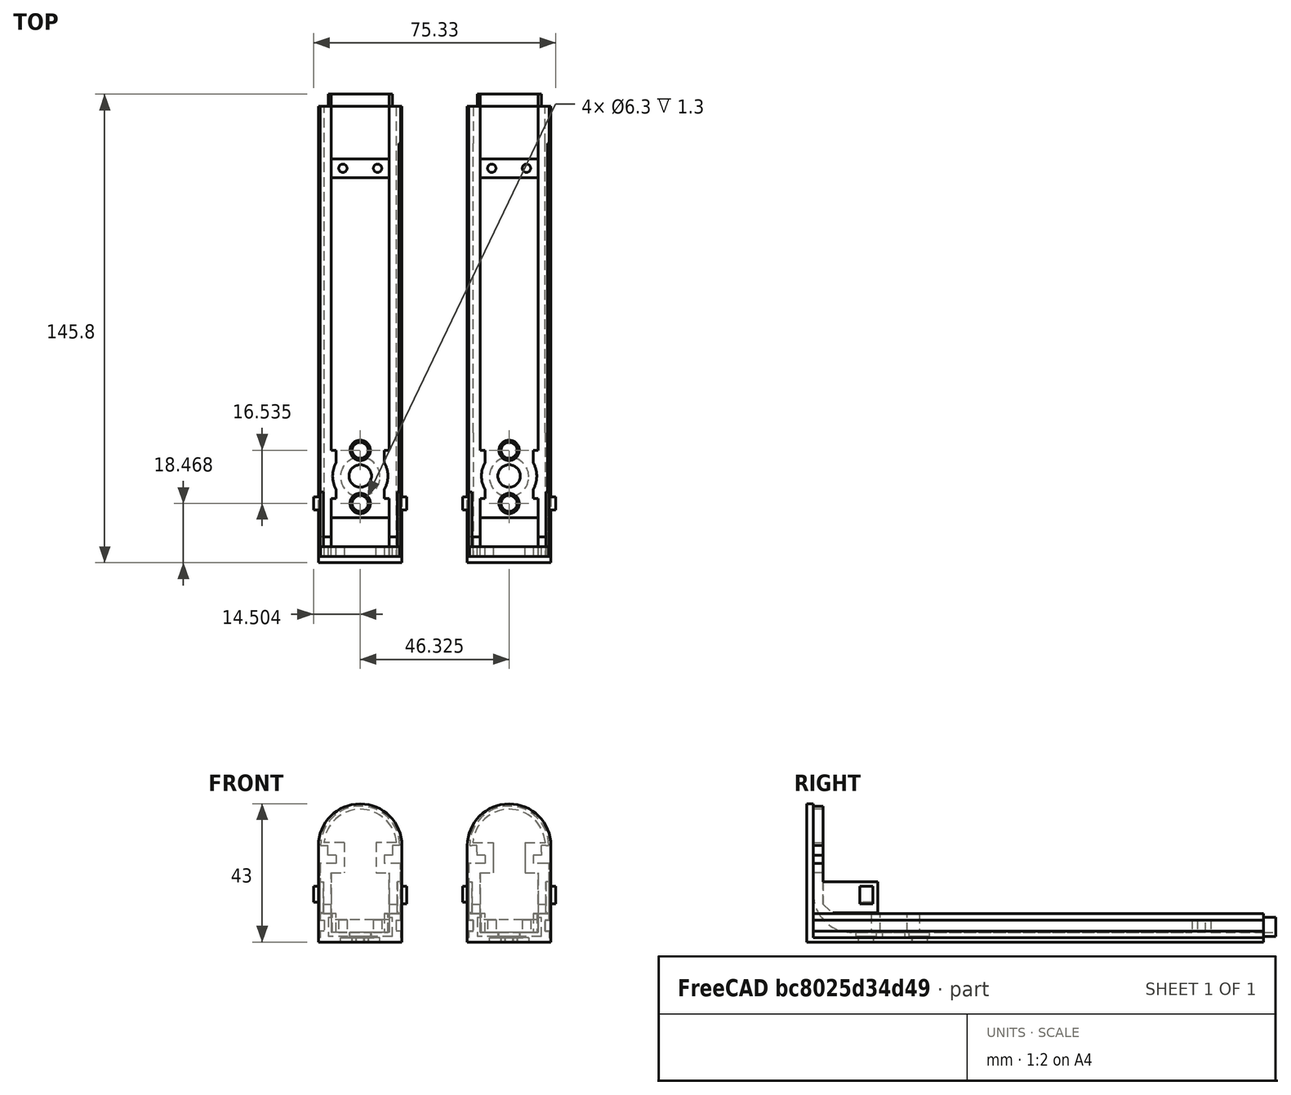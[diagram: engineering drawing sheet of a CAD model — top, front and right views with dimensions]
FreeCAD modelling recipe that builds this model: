
FCSTD DOCUMENT  (FreeCAD 0.18.3R)
Label: lamp.rail.button.section
License: All rights reserved
LicenseURL: http://en.wikipedia.org/wiki/All_rights_reserved
objects: Part::Extrusion×123, Part::Part2DObjectPython×96, Part::Cut×48, Part::Feature×34, Part::MultiFuse×28, Part::FeaturePython×8
note: 337 computed .brp shape members not serialized (recipe doc carries the construction recipe); baked Part::Feature solids carry a one-line shape summary decoded from their .brp

FEATURE [Part::Part2DObjectPython] Wire  # Draft 2D object (typed FeaturePython)
  ChamferSize = 0
  Closed = true
  End = (0.21072,-23,0.864956)
  FilletRadius = 0
  Length = 84.1989
  MakeFace = true
  Placement = pos=(0.21072,-23,6.66496) rot=(1,0,0;1.5708rad)
  Points = (20) [(0,0,0),(-4.5,0,-7.10543e-15),(-4.5,-2,-3.55271e-15),(-3.25,-2,-3.55271e-15),(-3.25,-5.4,-3.55271e-15),(-4.5,-5.4,-3.55271e-15),+14 more]
  Start = (0.21072,-23,6.66496)
  Subdivisions = 0
FEATURE [Part::Extrusion] Extrude018
  Base = -> Wire
  Dir = (-1e-16,-1,2e-16)
  DirMode = 2
  FaceMakerClass = Part::FaceMakerBullseye
  LengthFwd = 50
  LengthRev = 0
  Placement = pos=(37.158,39.9631,-2.99945) rot=(0,0,1;0rad)
  Solid = false
  Symmetric = false
FEATURE [Part::Part2DObjectPython] Circle  # Draft 2D object (typed FeaturePython)
  FirstAngle = 0
  LastAngle = 0
  MakeFace = true
  Placement = pos=(44.8687,-8.03685,-2.1345) rot=(0,0,1;3.14159rad)
  Radius = 8.5
  Support = -> [Extrude018]
FEATURE [Part::Extrusion] Extrude019
  Base = -> Circle
  Dir = (0,2e-16,1)
  DirMode = 2
  FaceMakerClass = Part::FaceMakerBullseye
  LengthFwd = 10
  LengthRev = 0
  Solid = false
  Symmetric = false
FEATURE [Part::Cut] Cut003
  Base = -> Extrude018
  Tool = -> Extrude019
FEATURE [Part::Part2DObjectPython] Circle002  # Draft 2D object (typed FeaturePython)
  FirstAngle = 0
  LastAngle = 0
  MakeFace = true
  Placement = pos=(44.8687,4.96315,-2.1345) rot=(0,0,1;3.14159rad)
  Radius = 2.5
FEATURE [Part::Extrusion] Extrude020
  Base = -> Circle002
  Dir = (0,2e-16,1)
  DirMode = 2
  FaceMakerClass = Part::FaceMakerBullseye
  LengthFwd = -10
  LengthRev = 0
  Placement = pos=(0,-5,2.2e-15) rot=(0,0,1;0rad)
  Solid = false
  Symmetric = false
FEATURE [Part::Part2DObjectPython] Circle003  # Draft 2D object (typed FeaturePython)
  FirstAngle = 0
  LastAngle = 0
  MakeFace = true
  Placement = pos=(44.8687,-8.03685,-2.1345) rot=(0,0,1;3.14159rad)
  Radius = 3.5
FEATURE [Part::Extrusion] Extrude021
  Base = -> Circle003
  Dir = (0,2e-16,1)
  DirMode = 2
  FaceMakerClass = Part::FaceMakerBullseye
  LengthFwd = -10
  LengthRev = 0
  Solid = false
  Symmetric = false
FEATURE [Part::Cut] Cut004
  Base = -> Cut003
  Tool = -> Extrude020
FEATURE [Part::Cut] Cut005
  Base = -> Cut004
  Tool = -> Extrude021
FEATURE [Part::Part2DObjectPython] Circle005  # Draft 2D object (typed FeaturePython)
  FirstAngle = 0
  LastAngle = 0
  MakeFace = true
  Placement = pos=(44.8687,-0.0368513,-2.1345) rot=(0,0,1;0rad)
  Radius = 3.1
FEATURE [Part::Part2DObjectPython] Circle004  # Draft 2D object (typed FeaturePython)
  FirstAngle = 0
  LastAngle = 0
  MakeFace = true
  Placement = pos=(44.8687,-8.16864,-5.13395) rot=(1,0,0;3.14159rad)
  Radius = 6
  Support = -> [Cut005]
FEATURE [Part::Extrusion] Extrude022
  Base = -> Circle004
  Dir = (0,-2e-16,-1)
  DirMode = 2
  FaceMakerClass = Part::FaceMakerBullseye
  LengthFwd = -1
  LengthRev = 0
  Solid = false
  Symmetric = false
FEATURE [Part::Cut] Cut
  Base = -> Cut005
  Tool = -> Extrude022
FEATURE [Part::Extrusion] Extrude
  Base = -> Circle005
  Dir = (0,0,1)
  DirMode = 2
  FaceMakerClass = Part::FaceMakerBullseye
  LengthFwd = -1.3
  LengthRev = 0
  Solid = false
  Symmetric = false
FEATURE [Part::Cut] Cut006
  Base = -> Cut
  Tool = -> Extrude
FEATURE [Part::Part2DObjectPython] Rectangle  # Draft 2D object (typed FeaturePython)
  ChamferSize = 0
  Columns = 1
  FilletRadius = 0
  Height = 5.8
  Length = 17
  MakeFace = true
  Placement = pos=(36.3687,-33.0369,-2.1345) rot=(1,0,0;1.5708rad)
  Rows = 1
  Support = -> [Cut006]
FEATURE [Part::Extrusion] Extrude023
  Base = -> Rectangle
  Dir = (1e-16,-1,-2e-16)
  DirMode = 2
  FaceMakerClass = Part::FaceMakerBullseye
  LengthFwd = -18
  LengthRev = 0
  Solid = false
  Symmetric = false
FEATURE [Part::Cut] Cut007
  Base = -> Cut006
  Tool = -> Extrude023
FEATURE [Part::Part2DObjectPython] Rectangle001  # Draft 2D object (typed FeaturePython)
  ChamferSize = 0
  Columns = 1
  FilletRadius = 0
  Height = 5.8
  Length = 17
  MakeFace = true
  Placement = pos=(36.3687,16.9631,-2.1345) rot=(1,0,0;1.5708rad)
  Rows = 1
FEATURE [Part::Extrusion] Extrude024
  Base = -> Rectangle001
  Dir = (0,-1,-2e-16)
  DirMode = 2
  FaceMakerClass = Part::FaceMakerBullseye
  LengthFwd = 17
  LengthRev = 0
  Solid = false
  Symmetric = false
FEATURE [Part::Cut] Cut008
  Base = -> Cut007
  Tool = -> Extrude024
FEATURE [Part::Part2DObjectPython] Rectangle003  # Draft 2D object (typed FeaturePython)
  ChamferSize = 0
  Columns = 1
  FilletRadius = 0
  Height = 16.2005
  Length = 24
  MakeFace = true
  Placement = pos=(32.8687,-33.0369,3.6655) rot=(1,0,0;1.5708rad)
  Rows = 1
FEATURE [Part::Extrusion] Extrude026
  Base = -> Rectangle003
  Dir = (1e-16,-1,-2e-16)
  DirMode = 2
  FaceMakerClass = Part::FaceMakerBullseye
  LengthFwd = -3
  LengthRev = 0
  Solid = false
  Symmetric = false
FEATURE [Part::Part2DObjectPython] Rectangle004  # Draft 2D object (typed FeaturePython)
  ChamferSize = 0
  Columns = 1
  FilletRadius = 0
  Height = 15.2
  Length = 22
  MakeFace = true
  Placement = pos=(55.8687,-30.0369,3.6655) rot=(0,0.707107,0.707107;3.14159rad)
  Rows = 1
FEATURE [Part::Extrusion] Extrude027
  Base = -> Rectangle004
  Dir = (-1e-16,1,2e-16)
  DirMode = 2
  FaceMakerClass = Part::FaceMakerBullseye
  LengthFwd = -3
  LengthRev = 0
  Solid = false
  Symmetric = false
FEATURE [Part::Cut] Cut009
  Base = -> Extrude026
  Tool = -> Extrude027
FEATURE [Part::Feature] Face002
  shape: bbox 2e-07 x 3 x 15.2 mm, 1 faces, 0 solids (baked)
FEATURE [Part::Extrusion] Extrusion002
  Base = -> Face002
  Dir = (-2.5,-2e-16,-2e-16)
  DirMode = 0
  FaceMakerClass = Part::FaceMakerBullseye
  LengthFwd = 0
  LengthRev = 0
  Solid = true
  Symmetric = false
FEATURE [Part::Feature] Face003
  shape: bbox 2e-07 x 3 x 15.2 mm, 1 faces, 0 solids (baked)
FEATURE [Part::Extrusion] Extrusion003
  Base = -> Face003
  Dir = (2.5,2e-16,2e-16)
  DirMode = 0
  FaceMakerClass = Part::FaceMakerBullseye
  LengthFwd = 0
  LengthRev = 0
  Solid = true
  Symmetric = false
FEATURE [Part::Part2DObjectPython] Rectangle039  # Draft 2D object (typed FeaturePython)
  ChamferSize = 0
  Columns = 1
  FilletRadius = 0
  Height = 1.4
  Length = 50
  MakeFace = true
  Placement = pos=(57.3687,-33.0369,-5.1345) rot=(0.57735,0.57735,0.57735;2.0944rad)
  Rows = 1
FEATURE [Part::Part2DObjectPython] Rectangle040  # Draft 2D object (typed FeaturePython)
  ChamferSize = 0
  Columns = 1
  FilletRadius = 0
  Height = 2
  Length = 50
  MakeFace = true
  Placement = pos=(32.8687,16.9631,1.6655) rot=(0.57735,-0.57735,-0.57735;2.0944rad)
  Rows = 1
FEATURE [Part::Extrusion] Extrude055
  Base = -> Rectangle040
  Dir = (-1,0,0)
  DirMode = 2
  FaceMakerClass = Part::FaceMakerBullseye
  LengthFwd = 0.5
  LengthRev = 0
  Solid = false
  Symmetric = false
FEATURE [Part::Part2DObjectPython] Rectangle041  # Draft 2D object (typed FeaturePython)
  ChamferSize = 0
  Columns = 1
  FilletRadius = 0
  Height = 1.99945
  Length = 50
  MakeFace = true
  Placement = pos=(56.8687,16.9631,1.6655) rot=(0.57735,-0.57735,-0.57735;2.0944rad)
  Rows = 1
FEATURE [Part::Extrusion] Extrude056
  Base = -> Rectangle041
  Dir = (-1,0,0)
  DirMode = 2
  FaceMakerClass = Part::FaceMakerBullseye
  LengthFwd = -0.5
  LengthRev = 0
  Solid = false
  Symmetric = false
FEATURE [Part::Part2DObjectPython] Rectangle042  # Draft 2D object (typed FeaturePython)
  ChamferSize = 0
  Columns = 1
  FilletRadius = 0
  Height = 2
  Length = 50
  MakeFace = true
  Placement = pos=(56.8687,16.9631,-3.7345) rot=(0.57735,-0.57735,-0.57735;2.0944rad)
  Rows = 1
FEATURE [Part::Extrusion] Extrude057
  Base = -> Rectangle042
  Dir = (-1,0,0)
  DirMode = 2
  FaceMakerClass = Part::FaceMakerBullseye
  LengthFwd = -0.5
  LengthRev = 0
  Solid = false
  Symmetric = false
FEATURE [Part::Part2DObjectPython] Rectangle043  # Draft 2D object (typed FeaturePython)
  ChamferSize = 0
  Columns = 1
  FilletRadius = 0
  Height = 2
  Length = 50
  MakeFace = true
  Placement = pos=(32.8687,16.9631,-3.7345) rot=(0.57735,-0.57735,-0.57735;2.0944rad)
  Rows = 1
FEATURE [Part::Extrusion] Extrude058
  Base = -> Rectangle043
  Dir = (-1,0,0)
  DirMode = 2
  FaceMakerClass = Part::FaceMakerBullseye
  LengthFwd = 0.5
  LengthRev = 0
  Solid = false
  Symmetric = false
FEATURE [Part::Part2DObjectPython] Rectangle044  # Draft 2D object (typed FeaturePython)
  ChamferSize = 0
  Columns = 1
  FilletRadius = 0
  Height = 1.39945
  Length = 50
  MakeFace = true
  Placement = pos=(32.3687,16.9631,-5.13395) rot=(0.57735,-0.57735,-0.57735;2.0944rad)
  Rows = 1
FEATURE [Part::Extrusion] Extrude059
  Base = -> Rectangle044
  Dir = (-1,0,0)
  DirMode = 2
  FaceMakerClass = Part::FaceMakerBullseye
  LengthFwd = 0.5
  LengthRev = 0
  Solid = false
  Symmetric = false
FEATURE [Part::Extrusion] Extrude060
  Base = -> Rectangle039
  Dir = (1,0,0)
  DirMode = 2
  FaceMakerClass = Part::FaceMakerBullseye
  LengthFwd = 0.5
  LengthRev = 0
  Solid = false
  Symmetric = false
FEATURE [Part::Feature] Face007
  shape: bbox 2e-07 x 3 x 16.2 mm, 1 faces, 0 solids (baked)
FEATURE [Part::Extrusion] Extrusion004
  Base = -> Face007
  Dir = (0.5,1e-16,0)
  DirMode = 0
  FaceMakerClass = Part::FaceMakerBullseye
  LengthFwd = 0
  LengthRev = 0
  Solid = true
  Symmetric = false
FEATURE [Part::Feature] Face009
  shape: bbox 2e-07 x 3 x 16.2 mm, 1 faces, 0 solids (baked)
FEATURE [Part::Extrusion] Extrusion005
  Base = -> Face009
  Dir = (-0.5,-1e-16,0)
  DirMode = 0
  FaceMakerClass = Part::FaceMakerBullseye
  LengthFwd = 0
  LengthRev = 0
  Solid = true
  Symmetric = false
FEATURE [Part::MultiFuse] Fusion
  Shapes = -> [Cut009,Extrusion004,Extrusion005]
FEATURE [Part::Part2DObjectPython] Rectangle045  # Draft 2D object (typed FeaturePython)
  ChamferSize = 0
  Columns = 1
  FilletRadius = 0
  Height = 25
  Length = 3
  MakeFace = true
  Placement = pos=(32.3687,-30.0369,19.8661) rot=(0,0,-1;1.5708rad)
  Rows = 1
FEATURE [Part::Extrusion] Extrude062
  Base = -> Rectangle045
  Dir = (-1e-16,-1e-16,1)
  DirMode = 2
  FaceMakerClass = Part::FaceMakerBullseye
  LengthFwd = -0.2
  LengthRev = 0
  Solid = false
  Symmetric = false
FEATURE [Part::Cut] Cut024
  Base = -> Fusion
  Tool = -> Extrude062
FEATURE [Part::Part2DObjectPython] Circle007  # Draft 2D object (typed FeaturePython)
  FirstAngle = 0
  LastAngle = 0
  MakeFace = true
  Placement = pos=(44.8687,-0.0368513,-5.13395) rot=(1,0,0;3.14159rad)
  Radius = 2.55
  Support = -> [Cut008]
FEATURE [Part::Extrusion] Extrude063
  Base = -> Circle007
  Dir = (0,-2e-16,-1)
  DirMode = 2
  FaceMakerClass = Part::FaceMakerBullseye
  LengthFwd = -11
  LengthRev = 0
  Solid = false
  Symmetric = false
FEATURE [Part::Part2DObjectPython] Wire001  # Draft 2D object (typed FeaturePython)
  ChamferSize = 0
  Closed = true
  End = (53.3687,-30.0369,3.6655)
  FilletRadius = 0
  Length = 10.2426
  MakeFace = true
  Placement = pos=(53.3687,-30.0369,6.6655) rot=(1,0,0;3.14159rad)
  Points = (3) [(0,0,0),(0,-3,3),(0,-1.06581e-14,3)]
  Start = (53.3687,-30.0369,6.6655)
  Subdivisions = 0
FEATURE [Part::Extrusion] Extrusion006
  Base = -> Wire001
  Dir = (4,-1e-16,0)
  DirMode = 0
  FaceMakerClass = Part::FaceMakerBullseye
  LengthFwd = 0
  LengthRev = 0
  Solid = true
  Symmetric = false
FEATURE [Part::Part2DObjectPython] Wire002  # Draft 2D object (typed FeaturePython)
  ChamferSize = 0
  Closed = true
  End = (32.3687,-30.0369,3.6655)
  FilletRadius = 0
  Length = 10.2426
  MakeFace = true
  Placement = pos=(32.3687,-30.0369,6.6655) rot=(1,0,0;3.14159rad)
  Points = (3) [(0,0,0),(0,-3,3),(0,-7.10543e-15,3)]
  Start = (32.3687,-30.0369,6.6655)
  Subdivisions = 0
FEATURE [Part::Extrusion] Extrusion007
  Base = -> Wire002
  Dir = (4,-1e-16,0)
  DirMode = 0
  FaceMakerClass = Part::FaceMakerBullseye
  LengthFwd = 0
  LengthRev = 0
  Solid = true
  Symmetric = false
FEATURE [Part::Cut] Cut025
  Base = -> Cut008
  Tool = -> Extrude063
FEATURE [Part::Feature] Face010
  Placement = pos=(37.158,39.9631,-2.99945) rot=(0,0,1;0rad)
  shape: bbox 2e-07 x 50 x 3.4 mm, 1 faces, 0 solids (baked)
FEATURE [Part::Extrusion] Extrusion008
  Base = -> Face010
  Dir = (-0.4,1e-16,0)
  DirMode = 0
  FaceMakerClass = Part::FaceMakerBullseye
  LengthFwd = 0
  LengthRev = 0
  Solid = true
  Symmetric = false
FEATURE [Part::Feature] Face011
  Placement = pos=(37.158,39.9631,-2.99945) rot=(0,0,1;0rad)
  shape: bbox 2e-07 x 50 x 3.4 mm, 1 faces, 0 solids (baked)
FEATURE [Part::Extrusion] Extrusion009
  Base = -> Face011
  Dir = (0.4,-1e-16,1e-16)
  DirMode = 0
  FaceMakerClass = Part::FaceMakerBullseye
  LengthFwd = 0
  LengthRev = 0
  Solid = true
  Symmetric = false
FEATURE [Part::Part2DObjectPython] Rectangle055  # Draft 2D object (typed FeaturePython)
  ChamferSize = 0
  Columns = 1
  FilletRadius = 0
  Height = 17
  Length = 0.5
  MakeFace = true
  Placement = pos=(35.8687,16.9631,3.6655) rot=(1,0,0;3.14159rad)
  Rows = 1
  Support = -> [Cut025]
FEATURE [Part::Extrusion] Extrude076
  Base = -> Rectangle055
  Dir = (0,-1e-16,-1)
  DirMode = 2
  FaceMakerClass = Part::FaceMakerBullseye
  LengthFwd = 5.8
  LengthRev = 0
  Solid = false
  Symmetric = false
FEATURE [Part::Cut] Cut030
  Base = -> Cut025
  Tool = -> Extrude076
FEATURE [Part::Part2DObjectPython] Rectangle056  # Draft 2D object (typed FeaturePython)
  ChamferSize = 0
  Columns = 1
  FilletRadius = 0
  Height = 17
  Length = 0.5
  MakeFace = true
  Placement = pos=(53.3687,-0.0368513,3.6655) rot=(0,0,1;0rad)
  Rows = 1
  Support = -> [Cut030]
FEATURE [Part::Extrusion] Extrude077
  Base = -> Rectangle056
  Dir = (1e-16,2e-16,1)
  DirMode = 2
  FaceMakerClass = Part::FaceMakerBullseye
  LengthFwd = -5.8
  LengthRev = 0
  Solid = false
  Symmetric = false
FEATURE [Part::Cut] Cut031
  Base = -> Cut030
  Tool = -> Extrude077
FEATURE [Part::Part2DObjectPython] Rectangle057  # Draft 2D object (typed FeaturePython)
  ChamferSize = 0
  Columns = 1
  FilletRadius = 0
  Height = 15.2
  Length = 18
  MakeFace = true
  Placement = pos=(53.8687,-15.0369,3.6655) rot=(0,0.707107,0.707107;3.14159rad)
  Rows = 1
FEATURE [Part::Extrusion] Extrusion010
  Base = -> Rectangle057
  Dir = (1.4e-15,-18,-4e-15)
  DirMode = 0
  FaceMakerClass = Part::FaceMakerBullseye
  LengthFwd = 0
  LengthRev = 0
  Solid = true
  Symmetric = false
FEATURE [Part::Feature] Face012
  shape: bbox 18 x 18 x 2e-07 mm, 1 faces, 0 solids (baked)
FEATURE [Part::Extrusion] Extrusion011
  Base = -> Face012
  Dir = (4e-16,1.3e-15,-5.8)
  DirMode = 0
  FaceMakerClass = Part::FaceMakerBullseye
  LengthFwd = 0
  LengthRev = 0
  Solid = true
  Symmetric = false
FEATURE [Part::MultiFuse] Fusion009
  Shapes = -> [Extrusion011,Extrusion010]
FEATURE [Part::MultiFuse] Fusion010
  Shapes = -> [Cut031,Extrusion003,Extrusion002]
FEATURE [Part::MultiFuse] Fusion011
  Shapes = -> [Fusion010,Extrusion006,Extrusion007]
FEATURE [Part::Cut] Cut032
  Base = -> Fusion011
  Tool = -> Fusion009
FEATURE [Part::Part2DObjectPython] Rectangle059  # Draft 2D object (typed FeaturePython)
  ChamferSize = 0
  Columns = 1
  FilletRadius = 0
  Height = 30
  Length = 26
  MakeFace = true
  Placement = pos=(31.8687,-34.4369,-5.13395) rot=(1,0,0;1.5708rad)
  Rows = 1
FEATURE [Part::Extrusion] Extrude079
  Base = -> Rectangle059
  Dir = (0,-1,-2e-16)
  DirMode = 2
  FaceMakerClass = Part::FaceMakerBullseye
  LengthFwd = -1.4
  LengthRev = 0
  Solid = false
  Symmetric = false
FEATURE [Part::Part2DObjectPython] Circle008  # Draft 2D object (typed FeaturePython)
  FirstAngle = 0
  LastAngle = 0
  MakeFace = true
  Placement = pos=(44.8687,-34.4369,24.8661) rot=(1,0,0;1.5708rad)
  Radius = 13
FEATURE [Part::Feature] Face013
  shape: bbox 20 x 3 x 3e-07 mm, 1 faces, 0 solids (baked)
FEATURE [Part::Extrusion] Extrusion012
  Base = -> Face013
  Dir = (0,-2e-16,2)
  DirMode = 0
  FaceMakerClass = Part::FaceMakerBullseye
  LengthFwd = 0
  LengthRev = 0
  Solid = true
  Symmetric = false
FEATURE [Part::Part2DObjectPython] Rectangle061  # Draft 2D object (typed FeaturePython)
  ChamferSize = 0
  Columns = 1
  FilletRadius = 0
  Height = 3
  Length = 23
  MakeFace = true
  Placement = pos=(33.3687,-30.0369,24.8661) rot=(1,0,0;3.14159rad)
  Rows = 1
FEATURE [Part::Part2DObjectPython] Rectangle062  # Draft 2D object (typed FeaturePython)
  ChamferSize = 0
  Columns = 1
  FilletRadius = 0
  Height = 3
  Length = 25
  MakeFace = true
  Placement = pos=(-3.36079,-33.0369,24.8661) rot=(0,0,1;0rad)
  Rows = 1
FEATURE [Part::Extrusion] Extrude083
  Base = -> Rectangle061
  Dir = (1.705e-13,-1e-16,-1)
  DirMode = 2
  FaceMakerClass = Part::FaceMakerBullseye
  LengthFwd = -1
  LengthRev = 0
  Solid = false
  Symmetric = false
FEATURE [Part::Feature] Face014
  shape: bbox 26 x 2e-07 x 30 mm, 1 faces, 0 solids (baked)
FEATURE [Part::Extrusion] Extrusion013
  Base = -> Face014
  Dir = (0,-0.6,-1e-16)
  DirMode = 0
  FaceMakerClass = Part::FaceMakerBullseye
  LengthFwd = 0
  LengthRev = 0
  Solid = true
  Symmetric = false
FEATURE [Part::Extrusion] Extrude080
  Base = -> Circle008
  Dir = (0,-1,-2e-16)
  DirMode = 2
  FaceMakerClass = Part::FaceMakerBullseye
  LengthFwd = -1.4
  LengthRev = 0
  Solid = false
  Symmetric = false
FEATURE [Part::Part2DObjectPython] Circle009  # Draft 2D object (typed FeaturePython)
  FirstAngle = 0
  LastAngle = 0
  MakeFace = true
  Placement = pos=(9.13921,-33.0369,24.8661) rot=(-1,0,0;1.5708rad)
  Radius = 12.3
  Support = -> [Extrude080]
FEATURE [Part::Part2DObjectPython] Circle010  # Draft 2D object (typed FeaturePython)
  FirstAngle = 0
  LastAngle = 0
  MakeFace = true
  Placement = pos=(9.13921,-33.0369,24.8661) rot=(-1,0,0;1.5708rad)
  Radius = 11.3
  Support = -> [Circle009]
FEATURE [Part::Feature] Face015
  Placement = pos=(44.8687,-34.4369,24.8661) rot=(1,0,0;1.5708rad)
  shape: bbox 26 x 2e-07 x 26 mm, 1 faces, 0 solids (baked)
FEATURE [Part::Extrusion] Extrusion014
  Base = -> Face015
  Dir = (0,-0.6,-1e-16)
  DirMode = 0
  FaceMakerClass = Part::FaceMakerBullseye
  LengthFwd = 0
  LengthRev = 0
  Solid = true
  Symmetric = false
FEATURE [Part::Feature] Face016
  shape: bbox 20 x 3 x 3e-07 mm, 1 faces, 0 solids (baked)
FEATURE [Part::Extrusion] Extrusion015
  Base = -> Face016
  Dir = (0,1e-16,-1)
  DirMode = 0
  FaceMakerClass = Part::FaceMakerBullseye
  LengthFwd = 0
  LengthRev = 0
  Solid = true
  Symmetric = false
FEATURE [Part::Extrusion] Extrude084
  Base = -> Circle009
  Dir = (0,1,2e-16)
  DirMode = 2
  FaceMakerClass = Part::FaceMakerBullseye
  LengthFwd = 3
  LengthRev = 0
  Solid = false
  Symmetric = false
FEATURE [Part::Extrusion] Extrude085
  Base = -> Circle010
  Dir = (0,1,2e-16)
  DirMode = 2
  FaceMakerClass = Part::FaceMakerBullseye
  LengthFwd = 3
  LengthRev = 0
  Solid = false
  Symmetric = false
FEATURE [Part::Cut] Cut033
  Base = -> Extrude084
  Tool = -> Extrude085
FEATURE [Part::FeaturePython] Slice001  # WARN: FeaturePython — macro-defined, semantics opaque (R4)
  Base = -> Cut033
  Mode = 1
  Tolerance = 0
  Tools = -> [Rectangle062]
FEATURE [Part::FeaturePython] Slice001_child1  label="Slice001.1"  # WARN: FeaturePython — macro-defined, semantics opaque (R4)
  Base = -> Slice001
  FilterType = 1
  Invert = false
  OverrideMaxVal = 0
  Placement = pos=(35.7295,7e-15,1.71e-13) rot=(0,0,1;0rad)
  WindowFrom = 80
  WindowTo = 100
  items = 1
FEATURE [Part::Part2DObjectPython] Rectangle063  # Draft 2D object (typed FeaturePython)
  ChamferSize = 0
  Columns = 1
  FilletRadius = 0
  Height = 0.3
  Length = 25
  MakeFace = true
  Placement = pos=(32.3687,-30.0369,19.6661) rot=(-1,0,0;1.5708rad)
  Rows = 1
  Support = -> [Cut024]
FEATURE [Part::Extrusion] Extrude086
  Base = -> Rectangle063
  Dir = (-1e-16,1,2e-16)
  DirMode = 2
  FaceMakerClass = Part::FaceMakerBullseye
  LengthFwd = -3
  LengthRev = 0
  Solid = false
  Symmetric = false
FEATURE [Part::Cut] Cut034
  Base = -> Cut024
  Tool = -> Extrude086
FEATURE [Part::Part2DObjectPython] Circle011  # Draft 2D object (typed FeaturePython)
  FirstAngle = 0
  LastAngle = 0
  MakeFace = true
  Placement = pos=(44.8687,-0.0368513,-5.13395) rot=(1,0,0;3.14159rad)
  Radius = 2.6
FEATURE [Part::Extrusion] Extrude087
  Base = -> Circle011
  Dir = (0,-2e-16,-1)
  DirMode = 2
  FaceMakerClass = Part::FaceMakerBullseye
  LengthFwd = -10
  LengthRev = 0
  Solid = false
  Symmetric = false
FEATURE [Part::Cut] Cut035
  Base = -> Cut032
  Tool = -> Extrude087
FEATURE [Part::Feature] Face017
  shape: bbox 22 x 3 x 2e-07 mm, 1 faces, 0 solids (baked)
FEATURE [Part::Extrusion] Extrusion016
  Base = -> Face017
  Dir = (0,1e-16,-0.499452)
  DirMode = 0
  FaceMakerClass = Part::FaceMakerBullseye
  LengthFwd = 0
  LengthRev = 0
  Solid = true
  Symmetric = false
FEATURE [Part::Part2DObjectPython] Circle012  # Draft 2D object (typed FeaturePython)
  FirstAngle = 0
  LastAngle = 0
  MakeFace = true
  Placement = pos=(44.8687,-8.17162,-5.13395) rot=(1,0,0;3.14159rad)
  Radius = 6.0021
FEATURE [Part::Extrusion] Extrude088
  Base = -> Circle012
  Dir = (0,-2e-16,-1)
  DirMode = 2
  FaceMakerClass = Part::FaceMakerBullseye
  LengthFwd = -1.3
  LengthRev = 0
  Solid = false
  Symmetric = false
FEATURE [Part::Cut] Cut036
  Base = -> Cut035
  Tool = -> Extrude088
FEATURE [Part::Part2DObjectPython] Rectangle014  # Draft 2D object (typed FeaturePython)
  ChamferSize = 0
  Columns = 1
  FilletRadius = 0
  Height = 2
  Length = 24
  MakeFace = true
  Placement = pos=(-4.28928,0,-0.735044) rot=(1,0,0;1.5708rad)
  Rows = 1
FEATURE [Part::Part2DObjectPython] Rectangle016  # Draft 2D object (typed FeaturePython)
  ChamferSize = 0
  Columns = 1
  FilletRadius = 0
  Height = 5.79945
  Length = 13
  MakeFace = true
  Placement = pos=(14.2107,0,0.865504) rot=(0,0.707107,0.707107;3.14159rad)
  Rows = 1
FEATURE [Part::Extrusion] Extrude089
  Base = -> Rectangle016
  Dir = (0,1,-2e-16)
  DirMode = 2
  FaceMakerClass = Part::FaceMakerBullseye
  LengthFwd = -23
  LengthRev = 0
  Solid = false
  Symmetric = false
FEATURE [Part::Part2DObjectPython] Rectangle013  # Draft 2D object (typed FeaturePython)
  ChamferSize = 0
  Columns = 1
  FilletRadius = 0
  Height = 2
  Length = 24
  MakeFace = true
  Placement = pos=(-4.28928,1.2e-15,4.66496) rot=(1,0,0;1.5708rad)
  Rows = 1
  Support = -> [Rectangle014]
FEATURE [Part::Extrusion] Extrude091
  Base = -> Rectangle014
  Dir = (0,-1,2e-16)
  DirMode = 2
  FaceMakerClass = Part::FaceMakerBullseye
  LengthFwd = 23
  LengthRev = 0
  Solid = false
  Symmetric = false
FEATURE [Part::Part2DObjectPython] Rectangle018  # Draft 2D object (typed FeaturePython)
  ChamferSize = 0
  Columns = 1
  FilletRadius = 0
  Height = 1.39945
  Length = 25
  MakeFace = true
  Placement = pos=(20.2107,-1e-15,-2.1345) rot=(0,0.707107,0.707107;3.14159rad)
  Rows = 1
FEATURE [Part::Extrusion] Extrude025
  Base = -> Rectangle018
  Dir = (0,1,-2e-16)
  DirMode = 2
  FaceMakerClass = Part::FaceMakerBullseye
  LengthFwd = -23
  LengthRev = 0
  Solid = false
  Symmetric = false
FEATURE [Part::Part2DObjectPython] Rectangle017  # Draft 2D object (typed FeaturePython)
  ChamferSize = 0
  Columns = 1
  FilletRadius = 0
  Height = 3.4
  Length = 21.5
  MakeFace = true
  Placement = pos=(-3.03928,0,1.26496) rot=(1,0,0;1.5708rad)
  Rows = 1
  Support = -> [Rectangle013]
FEATURE [Part::Extrusion] Extrude028
  Base = -> Rectangle017
  Dir = (0,-1,2e-16)
  DirMode = 2
  FaceMakerClass = Part::FaceMakerBullseye
  LengthFwd = 23
  LengthRev = 0
  Solid = false
  Symmetric = false
FEATURE [Part::Part2DObjectPython] Rectangle015  # Draft 2D object (typed FeaturePython)
  ChamferSize = 0
  Columns = 1
  FilletRadius = 0
  Height = 7.5
  Length = 7.85
  MakeFace = true
  Placement = pos=(3.96072,7.85,0.865504) rot=(0,0,-1;1.5708rad)
  Rows = 1
FEATURE [Part::Extrusion] Extrude031
  Base = -> Rectangle015
  Dir = (0,2e-16,1)
  DirMode = 2
  FaceMakerClass = Part::FaceMakerBullseye
  LengthFwd = -2
  LengthRev = 0
  Solid = false
  Symmetric = false
FEATURE [Part::Extrusion] Extrude029
  Base = -> Rectangle013
  Dir = (0,-1,2e-16)
  DirMode = 2
  FaceMakerClass = Part::FaceMakerBullseye
  LengthFwd = 23
  LengthRev = 0
  Solid = false
  Symmetric = false
FEATURE [Part::MultiFuse] Fusion003
  Shapes = -> [Extrude029,Extrude028,Extrude091,Extrude025]
FEATURE [Part::Cut] Cut038
  Base = -> Fusion003
  Tool = -> Extrude089
FEATURE [Part::Part2DObjectPython] Rectangle020  # Draft 2D object (typed FeaturePython)
  ChamferSize = 0
  Columns = 1
  FilletRadius = 0
  Height = 2.5
  Length = 8
  MakeFace = true
  Placement = pos=(3.71072,-23,-1.6345) rot=(1,0,0;1.5708rad)
  Rows = 1
  Support = -> [Cut038]
FEATURE [Part::Extrusion] Extrude030
  Base = -> Rectangle020
  Dir = (-1e-16,-1,2e-16)
  DirMode = 2
  FaceMakerClass = Part::FaceMakerBullseye
  LengthFwd = -8
  LengthRev = 0
  Solid = false
  Symmetric = false
FEATURE [Part::Cut] Cut037
  Base = -> Cut038
  Tool = -> Extrude030
FEATURE [Part::MultiFuse] Fusion002
  Shapes = -> [Cut037,Extrude031]
FEATURE [Part::Part2DObjectPython] Rectangle019  # Draft 2D object (typed FeaturePython)
  ChamferSize = 0
  Columns = 1
  FilletRadius = 0
  Height = 23
  Length = 15
  MakeFace = true
  Placement = pos=(15.2107,0,6.66496) rot=(0,0,1;3.14159rad)
  Rows = 1
  Support = -> [Fusion002]
FEATURE [Part::Extrusion] Extrude090
  Base = -> Rectangle019
  Dir = (0,2e-16,1)
  DirMode = 2
  FaceMakerClass = Part::FaceMakerBullseye
  LengthFwd = -5.8
  LengthRev = 0
  Solid = false
  Symmetric = false
FEATURE [Part::Cut] Cut010
  Base = -> Fusion002
  Placement = pos=(1.15935,45.2064,-9.8e-15) rot=(0,0,1;0rad)
  Tool = -> Extrude090
FEATURE [Part::Part2DObjectPython] Rectangle021  # Draft 2D object (typed FeaturePython)
  ChamferSize = 0
  Columns = 1
  FilletRadius = 0
  Height = 32.5147
  Length = 55.6938
  MakeFace = true
  Placement = pos=(36.717,33.7064,-13.163) rot=(0,0.707107,0.707107;3.14159rad)
  Rows = 1
  Support = -> [Cut010]
FEATURE [Part::FeaturePython] Slice  # WARN: FeaturePython — macro-defined, semantics opaque (R4)
  Base = -> Cut010
  Mode = 1
  Tolerance = 0
  Tools = -> [Rectangle021]
FEATURE [Part::FeaturePython] Slice_child0  label="Slice.0"  # WARN: FeaturePython — macro-defined, semantics opaque (R4)
  Base = -> Slice
  FilterType = 1
  Invert = false
  OverrideMaxVal = 0
  Placement = pos=(-30.6082,-11.7295,9e-16) rot=(0,0,1;0rad)
  WindowFrom = 80
  WindowTo = 100
  items = 0
FEATURE [Part::Feature] Face
  Placement = pos=(-29.4488,33.4769,-8.9e-15) rot=(0,0,1;0rad)
  shape: bbox 2e-07 x 7.85 x 2 mm, 1 faces, 0 solids (baked)
FEATURE [Part::Feature] Face001
  Placement = pos=(-29.4488,33.4769,-8.9e-15) rot=(0,0,1;0rad)
  shape: bbox 2e-07 x 7.85 x 2 mm, 1 faces, 0 solids (baked)
FEATURE [Part::Extrusion] Extrusion
  Base = -> Face
  Dir = (0.2,0,0)
  DirMode = 0
  FaceMakerClass = Part::FaceMakerBullseye
  LengthFwd = 0
  LengthRev = 0
  Solid = true
  Symmetric = false
FEATURE [Part::Extrusion] Extrusion001
  Base = -> Face001
  Dir = (-0.2,0,0)
  DirMode = 0
  FaceMakerClass = Part::FaceMakerBullseye
  LengthFwd = 0
  LengthRev = 0
  Solid = true
  Symmetric = false
FEATURE [Part::MultiFuse] Fusion004
  Shapes = -> [Extrusion,Extrusion001,Slice_child0]
FEATURE [Part::Part2DObjectPython] Rectangle024  # Draft 2D object (typed FeaturePython)
  ChamferSize = 0
  Columns = 1
  FilletRadius = 0
  Height = 17
  Length = 11.5
  MakeFace = true
  Placement = pos=(-30.2381,33.4769,0.864956) rot=(0,0,-1;1.5708rad)
  Rows = 1
FEATURE [Part::Extrusion] Extrude032
  Base = -> Rectangle024
  Dir = (0,0,1)
  DirMode = 2
  FaceMakerClass = Part::FaceMakerBullseye
  LengthFwd = 10
  LengthRev = 0
  Solid = false
  Symmetric = false
FEATURE [Part::Cut] Cut011
  Base = -> Fusion004
  Tool = -> Extrude032
FEATURE [Part::Part2DObjectPython] Rectangle028  # Draft 2D object (typed FeaturePython)
  ChamferSize = 0
  Columns = 1
  FilletRadius = 0
  Height = 4
  Length = 7.9
  MakeFace = true
  Placement = pos=(-25.6881,33.4769,-1.1345) rot=(0,0,1;0rad)
  Rows = 1
FEATURE [Part::Extrusion] Extrude040
  Base = -> Rectangle028
  Dir = (0,2e-16,1)
  DirMode = 2
  FaceMakerClass = Part::FaceMakerBullseye
  LengthFwd = 0.6
  LengthRev = 0
  Solid = false
  Symmetric = false
FEATURE [Part::Cut] Cut018
  Base = -> Cut011
  Tool = -> Extrude040
FEATURE [Part::Part2DObjectPython] Rectangle029  # Draft 2D object (typed FeaturePython)
  ChamferSize = 0
  Columns = 1
  FilletRadius = 0
  Height = 3.85
  Length = 7.9
  MakeFace = true
  Placement = pos=(-17.7881,37.4769,-1.1345) rot=(0,1,0;3.14159rad)
  Rows = 1
  Support = -> [Cut018]
FEATURE [Part::Extrusion] Extrude042
  Base = -> Rectangle029
  Dir = (0,0,-1)
  DirMode = 2
  FaceMakerClass = Part::FaceMakerBullseye
  LengthFwd = 0.1
  LengthRev = 0
  Solid = false
  Symmetric = false
FEATURE [Part::MultiFuse] Fusion006
  Shapes = -> [Cut018,Extrude042]
FEATURE [Part::Part2DObjectPython] Rectangle030  # Draft 2D object (typed FeaturePython)
  ChamferSize = 0
  Columns = 1
  FilletRadius = 0
  Height = 6.3
  Length = 1.1
  MakeFace = true
  Placement = pos=(-12.1381,33.4769,-0.735044) rot=(0,0.707107,0.707107;3.14159rad)
  Rows = 1
  Support = -> [Fusion006]
FEATURE [Part::Part2DObjectPython] Rectangle031  # Draft 2D object (typed FeaturePython)
  ChamferSize = 0
  Columns = 1
  FilletRadius = 0
  Height = 6.3
  Length = 1
  MakeFace = true
  Placement = pos=(-30.2381,33.4769,-0.735044) rot=(0,0.707107,0.707107;3.14159rad)
  Rows = 1
FEATURE [Part::Extrusion] Extrude048
  Base = -> Rectangle031
  Dir = (-2.5e-14,1,-2e-16)
  DirMode = 2
  FaceMakerClass = Part::FaceMakerBullseye
  LengthFwd = 3.8
  LengthRev = 0
  Solid = false
  Symmetric = false
FEATURE [Part::Part2DObjectPython] Rectangle036  # Draft 2D object (typed FeaturePython)
  ChamferSize = 0
  Columns = 1
  FilletRadius = 0
  Height = 3.85
  Length = 7.9
  MakeFace = true
  Placement = pos=(-17.7881,37.4769,-1.2345) rot=(0,1,0;3.14159rad)
  Rows = 1
FEATURE [Part::Extrusion] Extrude047
  Base = -> Rectangle030
  Dir = (-2.5e-14,1,-2e-16)
  DirMode = 2
  FaceMakerClass = Part::FaceMakerBullseye
  LengthFwd = 3.8
  LengthRev = 0
  Solid = false
  Symmetric = false
FEATURE [Part::Part2DObjectPython] Rectangle034  # Draft 2D object (typed FeaturePython)
  ChamferSize = 0
  Columns = 1
  FilletRadius = 0
  Height = 3.8
  Length = 1.1
  MakeFace = true
  Placement = pos=(-12.1381,33.4769,-0.735044) rot=(0,1,0;3.14159rad)
  Rows = 1
  Support = -> [Extrude047]
FEATURE [Part::Extrusion] Extrude049
  Base = -> Rectangle034
  Dir = (2.6e-14,0,-1)
  DirMode = 2
  FaceMakerClass = Part::FaceMakerBullseye
  LengthFwd = -0.1
  LengthRev = 0
  Solid = false
  Symmetric = false
FEATURE [Part::Cut] Cut021
  Base = -> Extrude047
  Placement = pos=(0.5,2.27e-13,0) rot=(0,0,1;0rad)
  Tool = -> Extrude049
FEATURE [Part::Part2DObjectPython] Rectangle035  # Draft 2D object (typed FeaturePython)
  ChamferSize = 0
  Columns = 1
  FilletRadius = 0
  Height = 3.8
  Length = 1
  MakeFace = true
  Placement = pos=(-30.2381,33.4769,-0.735044) rot=(0,1,0;3.14159rad)
  Rows = 1
  Support = -> [Fusion006]
FEATURE [Part::Extrusion] Extrude050
  Base = -> Rectangle035
  Dir = (2.6e-14,0,-1)
  DirMode = 2
  FaceMakerClass = Part::FaceMakerBullseye
  LengthFwd = -0.1
  LengthRev = 0
  Solid = false
  Symmetric = false
FEATURE [Part::Cut] Cut022
  Base = -> Extrude048
  Placement = pos=(-0.5,-7.1e-15,0) rot=(0,0,1;0rad)
  Tool = -> Extrude050
FEATURE [Part::Extrusion] Extrude051
  Base = -> Rectangle036
  Dir = (0,0,-1)
  DirMode = 2
  FaceMakerClass = Part::FaceMakerBullseye
  LengthFwd = 0.1
  LengthRev = 0
  Solid = false
  Symmetric = false
FEATURE [Part::Part2DObjectPython] Rectangle037  # Draft 2D object (typed FeaturePython)
  ChamferSize = 0
  Columns = 1
  FilletRadius = 0
  Height = 7.9
  Length = 4.1
  MakeFace = true
  Placement = pos=(-25.6881,33.4769,-0.534496) rot=(0.707107,0.707107,0;3.14159rad)
  Rows = 1
FEATURE [Part::Extrusion] Extrude052
  Base = -> Rectangle037
  Dir = (0,-3e-16,-1)
  DirMode = 2
  FaceMakerClass = Part::FaceMakerBullseye
  LengthFwd = 1
  LengthRev = 0
  Solid = false
  Symmetric = false
FEATURE [Part::Part2DObjectPython] Rectangle064  # Draft 2D object (typed FeaturePython)
  ChamferSize = 0
  Columns = 1
  FilletRadius = 0
  Height = 2
  Length = 11.5
  MakeFace = true
  Placement = pos=(-33.7381,33.4769,4.66496) rot=(0.57735,-0.57735,-0.57735;2.0944rad)
  Rows = 1
FEATURE [Part::Part2DObjectPython] Rectangle065  # Draft 2D object (typed FeaturePython)
  ChamferSize = 0
  Columns = 1
  FilletRadius = 0
  Height = 2
  Length = 11.5
  MakeFace = true
  Placement = pos=(-33.7381,33.4769,-0.735044) rot=(0.57735,-0.57735,-0.57735;2.0944rad)
  Rows = 1
FEATURE [Part::Extrusion] Extrude092
  Base = -> Rectangle065
  Dir = (-1,-2e-16,-2e-16)
  DirMode = 2
  FaceMakerClass = Part::FaceMakerBullseye
  LengthFwd = 0.5
  LengthRev = 0
  Solid = false
  Symmetric = false
FEATURE [Part::Extrusion] Extrude054
  Base = -> Rectangle064
  Dir = (-1,-2e-16,-2e-16)
  DirMode = 2
  FaceMakerClass = Part::FaceMakerBullseye
  LengthFwd = 0.5
  LengthRev = 0
  Solid = false
  Symmetric = false
FEATURE [Part::Part2DObjectPython] Rectangle066  # Draft 2D object (typed FeaturePython)
  ChamferSize = 0
  Columns = 1
  FilletRadius = 0
  Height = 2
  Length = 11.5
  MakeFace = true
  Placement = pos=(-9.73812,33.4769,-0.735044) rot=(0.57735,-0.57735,-0.57735;2.0944rad)
  Rows = 1
FEATURE [Part::Part2DObjectPython] Rectangle067  # Draft 2D object (typed FeaturePython)
  ChamferSize = 0
  Columns = 1
  FilletRadius = 0
  Height = 1.39945
  Length = 11.5
  MakeFace = true
  Placement = pos=(-34.2381,33.4769,-2.1345) rot=(0.57735,-0.57735,-0.57735;2.0944rad)
  Rows = 1
FEATURE [Part::Extrusion] Extrude093
  Base = -> Rectangle067
  Dir = (-1,-2e-16,-2e-16)
  DirMode = 2
  FaceMakerClass = Part::FaceMakerBullseye
  LengthFwd = 0.5
  LengthRev = 0
  Solid = false
  Symmetric = false
FEATURE [Part::Part2DObjectPython] Rectangle068  # Draft 2D object (typed FeaturePython)
  ChamferSize = 0
  Columns = 1
  FilletRadius = 0
  Height = 3.4
  Length = 11.5
  MakeFace = true
  Placement = pos=(-32.4881,33.4769,1.26496) rot=(0.57735,-0.57735,-0.57735;2.0944rad)
  Rows = 1
FEATURE [Part::Extrusion] Extrude094
  Base = -> Rectangle068
  Dir = (-1,-2e-16,-2e-16)
  DirMode = 2
  FaceMakerClass = Part::FaceMakerBullseye
  LengthFwd = 0.4
  LengthRev = 0
  Solid = false
  Symmetric = false
FEATURE [Part::Extrusion] Extrude095
  Base = -> Rectangle066
  Dir = (-1,-2e-16,-2e-16)
  DirMode = 2
  FaceMakerClass = Part::FaceMakerBullseye
  LengthFwd = -0.5
  LengthRev = 0
  Solid = false
  Symmetric = false
FEATURE [Part::Part2DObjectPython] Rectangle069  # Draft 2D object (typed FeaturePython)
  ChamferSize = 0
  Columns = 1
  FilletRadius = 0
  Height = 3.4
  Length = 11.5
  MakeFace = true
  Placement = pos=(-10.9881,33.4769,1.26496) rot=(0.57735,-0.57735,-0.57735;2.0944rad)
  Rows = 1
FEATURE [Part::Part2DObjectPython] Rectangle046  # Draft 2D object (typed FeaturePython)
  ChamferSize = 0
  Columns = 1
  FilletRadius = 0
  Height = 1.39945
  Length = 11.5
  MakeFace = true
  Placement = pos=(-9.23812,33.4769,-2.1345) rot=(0.57735,-0.57735,-0.57735;2.0944rad)
  Rows = 1
FEATURE [Part::Extrusion] Extrude061
  Base = -> Rectangle046
  Dir = (-1,-2e-16,-2e-16)
  DirMode = 2
  FaceMakerClass = Part::FaceMakerBullseye
  LengthFwd = -0.5
  LengthRev = 0
  Solid = false
  Symmetric = false
FEATURE [Part::Extrusion] Extrude097
  Base = -> Rectangle069
  Dir = (-1,-2e-16,-2e-16)
  DirMode = 2
  FaceMakerClass = Part::FaceMakerBullseye
  LengthFwd = -0.4
  LengthRev = 0
  Solid = false
  Symmetric = false
FEATURE [Part::Part2DObjectPython] Rectangle070  # Draft 2D object (typed FeaturePython)
  ChamferSize = 0
  Columns = 1
  FilletRadius = 0
  Height = 2
  Length = 11.5
  MakeFace = true
  Placement = pos=(-9.73812,33.4769,4.66496) rot=(0.57735,-0.57735,-0.57735;2.0944rad)
  Rows = 1
FEATURE [Part::Extrusion] Extrude096
  Base = -> Rectangle070
  Dir = (-1,-2e-16,-2e-16)
  DirMode = 2
  FaceMakerClass = Part::FaceMakerBullseye
  LengthFwd = -0.5
  LengthRev = 0
  Solid = false
  Symmetric = false
FEATURE [Part::Part2DObjectPython] Rectangle047  # Draft 2D object (typed FeaturePython)
  ChamferSize = 0
  Columns = 1
  FilletRadius = 0
  Height = 11.5
  Length = 18
  MakeFace = true
  Placement = pos=(-30.7381,21.9769,0.864956) rot=(0,0,1;0rad)
  Rows = 1
FEATURE [Part::Extrusion] Extrude098
  Base = -> Rectangle047
  Dir = (0,0,1)
  DirMode = 2
  FaceMakerClass = Part::FaceMakerBullseye
  LengthFwd = 10
  LengthRev = 0
  Solid = false
  Symmetric = false
FEATURE [Part::Cut] Cut039
  Base = -> Fusion006
  Tool = -> Extrude098
FEATURE [Part::MultiFuse] Fusion007
  Shapes = -> [Extrude051,Cut039]
FEATURE [Part::Cut] Cut026
  Base = -> Fusion007
  Tool = -> Extrude052
FEATURE [Part::MultiFuse] Fusion008
  Shapes = -> [Cut026,Extrude061,Extrude095,Extrude097,Extrude096,Extrude093,Extrude092,Extrude094,Extrude054]
FEATURE [Part::MultiFuse] Fusion012
  Placement = pos=(66.6069,-16.5138,-3) rot=(0,0,1;0rad)
  Shapes = -> [Cut021,Cut022,Fusion008]
FEATURE [Part::Part2DObjectPython] Rectangle073  # Draft 2D object (typed FeaturePython)
  ChamferSize = 0
  Columns = 1
  FilletRadius = 0
  Height = 10
  Length = 17
  MakeFace = true
  Placement = pos=(57.3687,-13.0369,3.6655) rot=(0.57735,-0.57735,-0.57735;2.0944rad)
  Rows = 1
FEATURE [Part::Part2DObjectPython] Rectangle074  # Draft 2D object (typed FeaturePython)
  ChamferSize = 0
  Columns = 1
  FilletRadius = 0
  Height = 10
  Length = 17
  MakeFace = true
  Placement = pos=(32.3687,-30.0369,3.6655) rot=(0.57735,0.57735,0.57735;2.0944rad)
  Rows = 1
FEATURE [Part::Part2DObjectPython] Circle013  # Draft 2D object (typed FeaturePython)
  FirstAngle = 0
  LastAngle = 0
  MakeFace = true
  Placement = pos=(44.8687,-0.0368513,-2.1345) rot=(0,0,1;0rad)
  Radius = 3.15
FEATURE [Part::Extrusion] Extrude103
  Base = -> Circle013
  Dir = (0,2e-16,1)
  DirMode = 2
  FaceMakerClass = Part::FaceMakerBullseye
  LengthFwd = -1.3
  LengthRev = 0
  Solid = false
  Symmetric = false
FEATURE [Part::Part2DObjectPython] Rectangle075  # Draft 2D object (typed FeaturePython)
  ChamferSize = 0
  Columns = 1
  FilletRadius = 0
  Height = 3
  Length = 10
  MakeFace = true
  Placement = pos=(49.8687,-33.0369,21.8661) rot=(0,1,0;3.14159rad)
  Rows = 1
FEATURE [Part::Extrusion] Extrusion017
  Base = -> Rectangle075
  Dir = (0,1e-16,-2.5)
  DirMode = 0
  FaceMakerClass = Part::FaceMakerBullseye
  LengthFwd = 0
  LengthRev = 0
  Solid = true
  Symmetric = false
FEATURE [Part::Part2DObjectPython] Rectangle076  # Draft 2D object (typed FeaturePython)
  ChamferSize = 0
  Columns = 1
  FilletRadius = 0
  Height = 6.5
  Length = 4
  MakeFace = true
  Placement = pos=(32.3687,-13.5369,6.2655) rot=(0.57735,-0.57735,-0.57735;2.0944rad)
  Rows = 1
FEATURE [Part::Extrusion] Extrude104
  Base = -> Rectangle076
  Dir = (-1,0,0)
  DirMode = 2
  FaceMakerClass = Part::FaceMakerBullseye
  LengthFwd = 1
  LengthRev = 0
  Solid = false
  Symmetric = false
FEATURE [Part::Part2DObjectPython] Rectangle077  # Draft 2D object (typed FeaturePython)
  ChamferSize = 0
  Columns = 1
  FilletRadius = 0
  Height = 6.5
  Length = 4
  MakeFace = true
  Placement = pos=(57.3687,-13.5369,6.26496) rot=(0.57735,-0.57735,-0.57735;2.0944rad)
  Rows = 1
FEATURE [Part::Extrusion] Extrude105
  Base = -> Rectangle077
  Dir = (-1,0,0)
  DirMode = 2
  FaceMakerClass = Part::FaceMakerBullseye
  LengthFwd = -1
  LengthRev = 0
  Solid = false
  Symmetric = false
FEATURE [Part::Extrusion] Extrude106
  Base = -> Rectangle074
  Dir = (1,0,0)
  DirMode = 2
  FaceMakerClass = Part::FaceMakerBullseye
  LengthFwd = 1
  LengthRev = 0
  Solid = false
  Symmetric = false
FEATURE [Part::Extrusion] Extrude107
  Base = -> Rectangle073
  Dir = (-1,0,0)
  DirMode = 2
  FaceMakerClass = Part::FaceMakerBullseye
  LengthFwd = 1
  LengthRev = 0
  Solid = false
  Symmetric = false
FEATURE [Part::Cut] Cut040
  Base = -> Cut036
  Tool = -> Extrude103
FEATURE [Part::MultiFuse] Fusion013
  Shapes = -> [Cut040,Extrude107,Extrude106,Extrude105,Extrude104,Extrusion015,Extrusion013,Extrude083,Extrusion016,Slice001_child1,Extrusion014,Extrude079,Fusion012,Extrusion009,Cut034,Extrusion008,Extrude058,Extrude057,Extrude060,Extrude055,Extrude056,Extrude059,Extrude080,Extrusion012,Extrusion017]
FEATURE [Part::Feature] Face018
  Placement = pos=(58.3687,-13.5369,6.26496) rot=(0.57735,-0.57735,-0.57735;2.0944rad)
  shape: bbox 4.243e-07 x 4 x 6.5 mm, 1 faces, 0 solids (baked)
FEATURE [Part::Extrusion] Extrusion018
  Base = -> Face018
  Dir = (1,0,0)
  DirMode = 0
  FaceMakerClass = Part::FaceMakerBullseye
  LengthFwd = 0
  LengthRev = 0
  Solid = true
  Symmetric = false
FEATURE [Part::Feature] Face019
  Placement = pos=(31.3687,-13.5369,6.2655) rot=(0.57735,-0.57735,-0.57735;2.0944rad)
  shape: bbox 4.243e-07 x 4 x 6.5 mm, 1 faces, 0 solids (baked)
FEATURE [Part::Extrusion] Extrusion019
  Base = -> Face019
  Dir = (-1,0,0)
  DirMode = 0
  FaceMakerClass = Part::FaceMakerBullseye
  LengthFwd = 0
  LengthRev = 0
  Solid = true
  Symmetric = false
FEATURE [Part::MultiFuse] Fusion014
  Shapes = -> [Extrusion019,Fusion013]
FEATURE [Part::MultiFuse] Fusion015
  Shapes = -> [Extrusion018,Fusion014]
FEATURE [Part::Part2DObjectPython] Rectangle078  # Draft 2D object (typed FeaturePython)
  ChamferSize = 0
  Columns = 1
  FilletRadius = 0
  Height = 6.5
  Length = 2
  MakeFace = true
  Placement = pos=(57.3687,-17.5369,6.26496) rot=(1,0,0;1.5708rad)
  Rows = 1
  Support = -> [Fusion015]
FEATURE [Part::Extrusion] Extrude108
  Base = -> Rectangle078
  Dir = (0,-1,2e-16)
  DirMode = 2
  FaceMakerClass = Part::FaceMakerBullseye
  LengthFwd = 1
  LengthRev = 0
  Solid = false
  Symmetric = false
FEATURE [Part::Part2DObjectPython] Rectangle079  # Draft 2D object (typed FeaturePython)
  ChamferSize = 0
  Columns = 1
  FilletRadius = 0
  Height = 6.5
  Length = 2
  MakeFace = true
  Placement = pos=(57.3687,-13.5369,6.26496) rot=(1,0,0;1.5708rad)
  Rows = 1
FEATURE [Part::Extrusion] Extrude109
  Base = -> Rectangle079
  Dir = (0,-1,2e-16)
  DirMode = 2
  FaceMakerClass = Part::FaceMakerBullseye
  LengthFwd = 1
  LengthRev = 0
  Solid = false
  Symmetric = false
FEATURE [Part::Cut] Cut041
  Base = -> Fusion015
  Tool = -> Extrude109
FEATURE [Part::MultiFuse] Fusion016
  Shapes = -> [Cut041,Extrude108]
FEATURE [Part::Part2DObjectPython] Rectangle080  # Draft 2D object (typed FeaturePython)
  ChamferSize = 0
  Columns = 1
  FilletRadius = 0
  Height = 6.5
  Length = 2
  MakeFace = true
  Placement = pos=(30.3687,-17.5369,6.2655) rot=(1,0,0;1.5708rad)
  Rows = 1
FEATURE [Part::Extrusion] Extrude110
  Base = -> Rectangle080
  Dir = (0,-1,2e-16)
  DirMode = 2
  FaceMakerClass = Part::FaceMakerBullseye
  LengthFwd = 1
  LengthRev = 0
  Solid = false
  Symmetric = false
FEATURE [Part::MultiFuse] Fusion017
  Shapes = -> [Extrude110,Fusion016]
FEATURE [Part::Part2DObjectPython] Rectangle081  # Draft 2D object (typed FeaturePython)
  ChamferSize = 0
  Columns = 1
  FilletRadius = 0
  Height = 6.5
  Length = 2
  MakeFace = true
  Placement = pos=(30.3687,-13.5369,6.2655) rot=(1,0,0;1.5708rad)
  Rows = 1
FEATURE [Part::Extrusion] Extrude111
  Base = -> Rectangle081
  Dir = (0,-1,2e-16)
  DirMode = 2
  FaceMakerClass = Part::FaceMakerBullseye
  LengthFwd = 1
  LengthRev = 0
  Solid = false
  Symmetric = false
FEATURE [Part::Cut] Cut042
  Base = -> Fusion017
  Tool = -> Extrude111
FEATURE [Part::Part2DObjectPython] Circle014  # Draft 2D object (typed FeaturePython)
  FirstAngle = 0
  LastAngle = 0
  MakeFace = true
  Placement = pos=(44.8687,-8.03685,3.6655) rot=(0,0,1;0rad)
  Radius = 8.6
FEATURE [Part::Extrusion] Extrude112
  Base = -> Circle014
  Dir = (1e-16,2e-16,1)
  DirMode = 2
  FaceMakerClass = Part::FaceMakerBullseye
  LengthFwd = -5.8
  LengthRev = 0
  Solid = false
  Symmetric = false
FEATURE [Part::Cut] Cut043
  Base = -> Cut042
  Tool = -> Extrude112
FEATURE [Part::Feature] Face020
  shape: bbox 18 x 3 x 3e-07 mm, 1 faces, 0 solids (baked)
FEATURE [Part::Extrusion] Extrusion020
  Base = -> Face020
  Dir = (2e-16,4e-16,-2)
  DirMode = 0
  FaceMakerClass = Part::FaceMakerBullseye
  LengthFwd = 0
  LengthRev = 0
  Solid = true
  Symmetric = false
FEATURE [Part::Feature] Cut032001  label="Cut044"
  Placement = pos=(101.993,44.5181,-2.99945) rot=(0,0,1;0rad)
  shape: bbox 26 x 19.35 x 8.799 mm, 36 faces (baked)
FEATURE [Part::Part2DObjectPython] Rectangle083  # Draft 2D object (typed FeaturePython)
  ChamferSize = 0
  Columns = 1
  FilletRadius = 0
  Height = 80.1
  Length = 80
  MakeFace = true
  Placement = pos=(26.4904,5.46315,-38.438) rot=(1,0,0;1.5708rad)
  Rows = 1
  Support = -> [Cut032001]
FEATURE [Part::FeaturePython] Slice003  # WARN: FeaturePython — macro-defined, semantics opaque (R4)
  Base = -> Cut043
  Mode = 1
  Tolerance = 0
  Tools = -> [Rectangle083]
FEATURE [Part::FeaturePython] Slice003_child0  label="Slice003.0"  # WARN: FeaturePython — macro-defined, semantics opaque (R4)
  Base = -> Slice003
  FilterType = 1
  Invert = false
  OverrideMaxVal = 0
  WindowFrom = 80
  WindowTo = 100
  items = 0
FEATURE [Part::Feature] Face021
  shape: bbox 26 x 4.243e-07 x 8.8 mm, 1 faces, 0 solids (baked)
FEATURE [Part::Extrusion] Extrusion021
  Base = -> Face021
  Dir = (2.26e-14,59.5,5.153e-13)
  DirMode = 0
  FaceMakerClass = Part::FaceMakerBullseye
  LengthFwd = 0
  LengthRev = 0
  Solid = true
  Symmetric = false
FEATURE [Part::Part2DObjectPython] Rectangle084  # Draft 2D object (typed FeaturePython)
  ChamferSize = 0
  Columns = 1
  FilletRadius = 0
  Height = 7.4
  Length = 98
  MakeFace = true
  Placement = pos=(32.3687,64.9631,-3.7345) rot=(0.57735,-0.57735,-0.57735;2.0944rad)
  Rows = 1
FEATURE [Part::Extrusion] Extrusion022
  Base = -> Rectangle084
  Dir = (0.5,0,0)
  DirMode = 0
  FaceMakerClass = Part::FaceMakerBullseye
  LengthFwd = 0
  LengthRev = 0
  Solid = true
  Symmetric = false
FEATURE [Part::MultiFuse] Fusion018
  Shapes = -> [Slice003_child0,Extrusion021]
FEATURE [Part::Cut] Cut032002
  Base = -> Fusion018
  Tool = -> Extrusion022
FEATURE [Part::Part2DObjectPython] Rectangle085  # Draft 2D object (typed FeaturePython)
  ChamferSize = 0
  Columns = 1
  FilletRadius = 0
  Height = 7.4
  Length = 98
  MakeFace = true
  Placement = pos=(57.3687,64.9631,-3.7345) rot=(0.57735,-0.57735,-0.57735;2.0944rad)
  Rows = 1
  Support = -> [Cut032002]
FEATURE [Part::Extrusion] Extrusion023
  Base = -> Rectangle085
  Dir = (-0.5,0,0)
  DirMode = 0
  FaceMakerClass = Part::FaceMakerBullseye
  LengthFwd = 0
  LengthRev = 0
  Solid = true
  Symmetric = false
FEATURE [Part::Cut] Cut032003
  Base = -> Cut032002
  Tool = -> Extrusion023
FEATURE [Part::Part2DObjectPython] Rectangle086  # Draft 2D object (typed FeaturePython)
  ChamferSize = 0
  Columns = 1
  FilletRadius = 0
  Height = 2
  Length = 4
  MakeFace = true
  Placement = pos=(32.3687,-18.5369,12.7655) rot=(0,0,1;1.5708rad)
  Rows = 1
  Support = -> [Cut032003]
FEATURE [Part::Extrusion] Extrude113
  Base = -> Rectangle086
  Dir = (0,0,1)
  DirMode = 2
  FaceMakerClass = Part::FaceMakerBullseye
  LengthFwd = -1
  LengthRev = 0
  Solid = false
  Symmetric = false
FEATURE [Part::Cut] Cut032004
  Base = -> Cut032003
  Tool = -> Extrude113
FEATURE [Part::Part2DObjectPython] Rectangle087  # Draft 2D object (typed FeaturePython)
  ChamferSize = 0
  Columns = 1
  FilletRadius = 0
  Height = 2
  Length = 4
  MakeFace = true
  Placement = pos=(59.3687,-18.5369,12.765) rot=(0,0,1;1.5708rad)
  Rows = 1
FEATURE [Part::Extrusion] Extrude114
  Base = -> Rectangle087
  Dir = (0,0,1)
  DirMode = 2
  FaceMakerClass = Part::FaceMakerBullseye
  LengthFwd = -1
  LengthRev = 0
  Solid = false
  Symmetric = false
FEATURE [Part::Cut] Cut032005
  Base = -> Cut032004
  Tool = -> Extrude114
FEATURE [Part::Part2DObjectPython] Rectangle088  # Draft 2D object (typed FeaturePython)
  ChamferSize = 0
  Columns = 1
  FilletRadius = 0
  Height = 0.3
  Length = 14
  MakeFace = true
  Placement = pos=(33.3687,-27.0369,3.6655) rot=(0.57735,0.57735,0.57735;2.0944rad)
  Rows = 1
FEATURE [Part::Extrusion] Extrude115
  Base = -> Rectangle088
  Dir = (1,0,0)
  DirMode = 2
  FaceMakerClass = Part::FaceMakerBullseye
  LengthFwd = -10
  LengthRev = 0
  Solid = false
  Symmetric = false
FEATURE [Part::Cut] Cut032006
  Base = -> Cut032005
  Tool = -> Extrude115
FEATURE [Part::Part2DObjectPython] Rectangle089  # Draft 2D object (typed FeaturePython)
  ChamferSize = 0
  Columns = 1
  FilletRadius = 0
  Height = 0.3
  Length = 14
  MakeFace = true
  Placement = pos=(56.3687,-13.0369,3.6655) rot=(0.57735,-0.57735,-0.57735;2.0944rad)
  Rows = 1
  Support = -> [Cut032006]
FEATURE [Part::Extrusion] Extrude116
  Base = -> Rectangle089
  Dir = (-1,0,0)
  DirMode = 2
  FaceMakerClass = Part::FaceMakerBullseye
  LengthFwd = -10
  LengthRev = 0
  Solid = false
  Symmetric = false
FEATURE [Part::Cut] Cut032007
  Base = -> Cut032006
  Tool = -> Extrude116
FEATURE [Part::Part2DObjectPython] Circle015  # Draft 2D object (typed FeaturePython)
  FirstAngle = 0
  LastAngle = 0
  MakeFace = true
  Placement = pos=(44.8687,-0.0368513,-3.4345) rot=(0,0,1;0rad)
  Radius = 2.6
FEATURE [Part::Part2DObjectPython] Circle016  # Draft 2D object (typed FeaturePython)
  FirstAngle = 0
  LastAngle = 0
  MakeFace = true
  Placement = pos=(44.8687,-0.0368513,-3.4345) rot=(0,0,1;0rad)
  Radius = 2.5
  Support = -> [Circle015]
FEATURE [Part::Extrusion] Extrude117
  Base = -> Circle015
  Dir = (0,0,1)
  DirMode = 2
  FaceMakerClass = Part::FaceMakerBullseye
  LengthFwd = -1.7
  LengthRev = 0
  Solid = false
  Symmetric = false
FEATURE [Part::Extrusion] Extrude118
  Base = -> Circle016
  Dir = (0,0,1)
  DirMode = 2
  FaceMakerClass = Part::FaceMakerBullseye
  LengthFwd = -1.7
  LengthRev = 0
  Solid = false
  Symmetric = false
FEATURE [Part::Cut] Cut032008
  Base = -> Extrude117
  Tool = -> Extrude118
FEATURE [Part::MultiFuse] Fusion019
  Shapes = -> [Cut032008,Cut032007]
FEATURE [Part::Part2DObjectPython] Circle017  # Draft 2D object (typed FeaturePython)
  FirstAngle = 0
  LastAngle = 0
  MakeFace = true
  Placement = pos=(44.8687,-8.30442,-3.83395) rot=(1,0,0;3.14159rad)
  Radius = 6.13197
FEATURE [Part::Extrusion] Extrude119
  Base = -> Circle017
  Dir = (0,0,-1)
  DirMode = 2
  FaceMakerClass = Part::FaceMakerBullseye
  LengthFwd = 10
  LengthRev = 0
  Solid = false
  Symmetric = false
FEATURE [Part::Cut] Cut032009
  Base = -> Fusion019
  Tool = -> Extrude119
FEATURE [Part::Part2DObjectPython] Rectangle090  # Draft 2D object (typed FeaturePython)
  ChamferSize = 0
  Columns = 1
  FilletRadius = 0
  Height = 50
  Length = 30
  MakeFace = true
  Placement = pos=(73.8687,9.96315,-2.1345) rot=(0,0,1;1.5708rad)
  Rows = 1
  Support = -> [Cut032009]
FEATURE [Part::Extrusion] Extrude120
  Base = -> Rectangle090
  Dir = (0,-8.7e-15,1)
  DirMode = 2
  FaceMakerClass = Part::FaceMakerBullseye
  LengthFwd = 10
  LengthRev = 0
  Placement = pos=(-1.5,-3.6e-14,3.8) rot=(0,0,1;0rad)
  Solid = false
  Symmetric = false
FEATURE [Part::MultiFuse] Fusion020
  Shapes = -> [Cut032001,Extrusion020]
FEATURE [Part::MultiFuse] Fusion021
  Shapes = -> [Fusion020,Cut032009]
FEATURE [Part::Feature] Face022
  shape: bbox 4.243e-07 x 98 x 2 mm, 1 faces, 0 solids (baked)
FEATURE [Part::Extrusion] Extrusion024
  Base = -> Face022
  Dir = (-0.5,0,0)
  DirMode = 0
  FaceMakerClass = Part::FaceMakerBullseye
  LengthFwd = 0
  LengthRev = 0
  Solid = true
  Symmetric = false
FEATURE [Part::Feature] Face023
  shape: bbox 4.243e-07 x 11.5 x 2 mm, 1 faces, 0 solids (baked)
FEATURE [Part::Extrusion] Extrusion025
  Base = -> Face023
  Dir = (-0.5,0,0)
  DirMode = 0
  FaceMakerClass = Part::FaceMakerBullseye
  LengthFwd = 0
  LengthRev = 0
  Solid = true
  Symmetric = false
FEATURE [Part::Feature] Face025
  shape: bbox 4.243e-07 x 98 x 2 mm, 1 faces, 0 solids (baked)
FEATURE [Part::Extrusion] Extrusion026
  Base = -> Face025
  Dir = (0.5,0,0)
  DirMode = 0
  FaceMakerClass = Part::FaceMakerBullseye
  LengthFwd = 0
  LengthRev = 0
  Solid = true
  Symmetric = false
FEATURE [Part::Feature] Face026
  shape: bbox 4.243e-07 x 98 x 1.999 mm, 1 faces, 0 solids (baked)
FEATURE [Part::Extrusion] Extrusion027
  Base = -> Face026
  Dir = (0.5,0,0)
  DirMode = 0
  FaceMakerClass = Part::FaceMakerBullseye
  LengthFwd = 0
  LengthRev = 0
  Solid = true
  Symmetric = false
FEATURE [Part::Feature] Face027
  shape: bbox 4.243e-07 x 11.5 x 2 mm, 1 faces, 0 solids (baked)
FEATURE [Part::Extrusion] Extrusion028
  Base = -> Face027
  Dir = (0.5,0,0)
  DirMode = 0
  FaceMakerClass = Part::FaceMakerBullseye
  LengthFwd = 0
  LengthRev = 0
  Solid = true
  Symmetric = false
FEATURE [Part::Feature] Face028
  shape: bbox 4.243e-07 x 11.5 x 2 mm, 1 faces, 0 solids (baked)
FEATURE [Part::Extrusion] Extrusion029
  Base = -> Face028
  Dir = (0.5,0,0)
  DirMode = 0
  FaceMakerClass = Part::FaceMakerBullseye
  LengthFwd = 0
  LengthRev = 0
  Solid = true
  Symmetric = false
FEATURE [Part::Feature] Face029
  shape: bbox 4.243e-07 x 98 x 2 mm, 1 faces, 0 solids (baked)
FEATURE [Part::Extrusion] Extrusion030
  Base = -> Face029
  Dir = (-0.5,0,0)
  DirMode = 0
  FaceMakerClass = Part::FaceMakerBullseye
  LengthFwd = 0
  LengthRev = 0
  Solid = true
  Symmetric = false
FEATURE [Part::Feature] Face030
  shape: bbox 4.243e-07 x 11.5 x 2 mm, 1 faces, 0 solids (baked)
FEATURE [Part::Extrusion] Extrusion031
  Base = -> Face030
  Dir = (-0.5,0,0)
  DirMode = 0
  FaceMakerClass = Part::FaceMakerBullseye
  LengthFwd = 0
  LengthRev = 0
  Solid = true
  Symmetric = false
FEATURE [Part::Part2DObjectPython] Rectangle091  # Draft 2D object (typed FeaturePython)
  ChamferSize = 0
  Columns = 1
  FilletRadius = 0
  Height = 4
  Length = 2
  MakeFace = true
  Placement = pos=(30.3687,-14.5369,6.2655) rot=(1,0,0;3.14159rad)
  Rows = 1
  Support = -> [Fusion021]
FEATURE [Part::Extrusion] Extrude121
  Base = -> Rectangle091
  Dir = (0,0,-1)
  DirMode = 2
  FaceMakerClass = Part::FaceMakerBullseye
  LengthFwd = -0.5
  LengthRev = 0
  Solid = false
  Symmetric = false
FEATURE [Part::Cut] Cut032010
  Base = -> Fusion021
  Tool = -> Extrude121
FEATURE [Part::Part2DObjectPython] Rectangle092  # Draft 2D object (typed FeaturePython)
  ChamferSize = 0
  Columns = 1
  FilletRadius = 0
  Height = 4
  Length = 2
  MakeFace = true
  Placement = pos=(57.3687,-14.5369,6.26496) rot=(1,0,0;3.14159rad)
  Rows = 1
FEATURE [Part::Extrusion] Extrude122
  Base = -> Rectangle092
  Dir = (0,0,-1)
  DirMode = 2
  FaceMakerClass = Part::FaceMakerBullseye
  LengthFwd = 0.5
  LengthRev = 0
  Solid = false
  Symmetric = false
FEATURE [Part::MultiFuse] Fusion022
  Shapes = -> [Extrusion026,Extrusion031,Extrusion027,Extrusion030,Extrusion028,Extrusion029,Extrusion024,Extrusion025]
FEATURE [Part::Part2DObjectPython] Circle021  # Draft 2D object (typed FeaturePython)
  FirstAngle = 0
  LastAngle = 0
  MakeFace = true
  Placement = pos=(44.8687,-16.572,-5.13395) rot=(1,0,0;3.14159rad)
  Radius = 2.5
FEATURE [Part::Extrusion] Extrude123
  Base = -> Circle021
  Dir = (0,-2e-16,-1)
  DirMode = 2
  FaceMakerClass = Part::FaceMakerBullseye
  LengthFwd = -10
  LengthRev = 0
  Solid = false
  Symmetric = false
FEATURE [Part::Part2DObjectPython] Circle023  # Draft 2D object (typed FeaturePython)
  FirstAngle = 0
  LastAngle = 0
  MakeFace = true
  Placement = pos=(44.8687,-16.572,-2.1345) rot=(0,0,1;0rad)
  Radius = 3.15
FEATURE [Part::Extrusion] Extrude124
  Base = -> Circle023
  Dir = (0,0,1)
  DirMode = 2
  FaceMakerClass = Part::FaceMakerBullseye
  LengthFwd = -1.3
  LengthRev = 0
  Solid = false
  Symmetric = false
FEATURE [Part::Feature] Face031
  shape: bbox 4.243e-07 x 3 x 2.5 mm, 1 faces, 0 solids (baked)
FEATURE [Part::Extrusion] Extrusion032
  Base = -> Face031
  Dir = (-2.5,0,0)
  DirMode = 0
  FaceMakerClass = Part::FaceMakerBullseye
  LengthFwd = 0
  LengthRev = 0
  Solid = true
  Symmetric = false
FEATURE [Part::Feature] Face032
  shape: bbox 4.243e-07 x 3 x 2.5 mm, 1 faces, 0 solids (baked)
FEATURE [Part::Extrusion] Extrusion033
  Base = -> Face032
  Dir = (2.5,0,0)
  DirMode = 0
  FaceMakerClass = Part::FaceMakerBullseye
  LengthFwd = 0
  LengthRev = 0
  Solid = true
  Symmetric = false
FEATURE [Part::Part2DObjectPython] Rectangle096  # Draft 2D object (typed FeaturePython)
  ChamferSize = 0
  Columns = 1
  FilletRadius = 0
  Height = 3
  Length = 10
  MakeFace = true
  Placement = pos=(49.8687,-30.0369,25.8661) rot=(0,0,1;3.14159rad)
  Rows = 1
FEATURE [Part::Extrusion] Extrude125
  Base = -> Rectangle096
  Dir = (-1.65e-13,0,1)
  DirMode = 2
  FaceMakerClass = Part::FaceMakerBullseye
  LengthFwd = -20
  LengthRev = 0
  Solid = false
  Symmetric = false
FEATURE [Part::Part2DObjectPython] Rectangle098  # Draft 2D object (typed FeaturePython)
  ChamferSize = 0
  Columns = 1
  FilletRadius = 0
  Height = 4
  Length = 2
  MakeFace = true
  Placement = pos=(30.3687,-18.5369,11.7655) rot=(0,0,1;0rad)
  Rows = 1
FEATURE [Part::Extrusion] Extrude127
  Base = -> Rectangle098
  Dir = (0,0,1)
  DirMode = 2
  FaceMakerClass = Part::FaceMakerBullseye
  LengthFwd = 0.5
  LengthRev = 0
  Solid = false
  Symmetric = false
FEATURE [Part::Part2DObjectPython] Rectangle099  # Draft 2D object (typed FeaturePython)
  ChamferSize = 0
  Columns = 1
  FilletRadius = 0
  Height = 4
  Length = 2
  MakeFace = true
  Placement = pos=(30.3687,-14.5369,6.7655) rot=(1,0,0;3.14159rad)
  Rows = 1
FEATURE [Part::Part2DObjectPython] Rectangle100  # Draft 2D object (typed FeaturePython)
  ChamferSize = 0
  Columns = 1
  FilletRadius = 0
  Height = 4
  Length = 2
  MakeFace = true
  Placement = pos=(57.3687,-14.5369,6.26496) rot=(1,0,0;3.14159rad)
  Rows = 1
FEATURE [Part::Extrusion] Extrude128
  Base = -> Rectangle099
  Dir = (0,0,-1)
  DirMode = 2
  FaceMakerClass = Part::FaceMakerBullseye
  LengthFwd = -0.5
  LengthRev = 0
  Solid = false
  Symmetric = false
FEATURE [Part::Extrusion] Extrude129
  Base = -> Rectangle100
  Dir = (0,0,-1)
  DirMode = 2
  FaceMakerClass = Part::FaceMakerBullseye
  LengthFwd = -0.5
  LengthRev = 0
  Solid = false
  Symmetric = false
FEATURE [Part::Feature] Face033
  shape: bbox 3.5 x 6.04e-07 x 2 mm, 1 faces, 0 solids (baked)
FEATURE [Part::Extrusion] Extrusion034
  Base = -> Face033
  Dir = (1.33e-14,30,2.601e-13)
  DirMode = 0
  FaceMakerClass = Part::FaceMakerBullseye
  LengthFwd = 0
  LengthRev = 0
  Solid = true
  Symmetric = false
FEATURE [Part::Feature] Face035
  shape: bbox 3.5 x 6.04e-07 x 2 mm, 1 faces, 0 solids (baked)
FEATURE [Part::Extrusion] Extrusion035
  Base = -> Face035
  Dir = (1.33e-14,30,2.601e-13)
  DirMode = 0
  FaceMakerClass = Part::FaceMakerBullseye
  LengthFwd = 0
  LengthRev = 0
  Solid = true
  Symmetric = false
FEATURE [Part::Cut] Cut032011
  Base = -> Cut032010
  Tool = -> Extrude122
FEATURE [Part::MultiFuse] Fusion023
  Shapes = -> [Cut032011,Fusion022]
FEATURE [Part::Cut] Cut032012
  Base = -> Fusion023
  Tool = -> Extrude120
FEATURE [Part::Cut] Cut032013
  Base = -> Cut032012
  Tool = -> Extrude123
FEATURE [Part::Cut] Cut032014
  Base = -> Cut032013
  Tool = -> Extrude124
FEATURE [Part::Cut] Cut032015
  Base = -> Cut032014
  Tool = -> Extrude125
FEATURE [Part::MultiFuse] Fusion024
  Shapes = -> [Extrusion032,Extrusion033,Cut032015]
FEATURE [Part::Part2DObjectPython] Rectangle097  # Draft 2D object (typed FeaturePython)
  ChamferSize = 0
  Columns = 1
  FilletRadius = 0
  Height = 4
  Length = 2
  MakeFace = true
  Placement = pos=(57.3687,-18.5369,11.765) rot=(0,0,1;0rad)
  Rows = 1
  Support = -> [Fusion024]
FEATURE [Part::Extrusion] Extrude126
  Base = -> Rectangle097
  Dir = (0,0,1)
  DirMode = 2
  FaceMakerClass = Part::FaceMakerBullseye
  LengthFwd = 0.5
  LengthRev = 0
  Solid = false
  Symmetric = false
FEATURE [Part::Cut] Cut032016
  Base = -> Fusion024
  Tool = -> Extrude128
FEATURE [Part::Cut] Cut032017
  Base = -> Cut032016
  Tool = -> Extrude129
FEATURE [Part::MultiFuse] Fusion025
  Shapes = -> [Extrude126,Extrude127,Extrusion034,Extrusion035,Cut032017]
FEATURE [Part::Feature] Cut047_solid001  label="Cut047 (Solid)001"
  Placement = pos=(66.6069,73.4862,-2.99945) rot=(0,0,1;0rad)
  shape: bbox 26 x 15.3 x 8.799 mm, 30 faces (baked)
FEATURE [Part::Part2DObjectPython] Rectangle101  # Draft 2D object (typed FeaturePython)
  ChamferSize = 0
  Columns = 1
  FilletRadius = 0
  Height = 30
  Length = 100
  MakeFace = true
  Placement = pos=(3.86875,5.46315,18.665) rot=(-1,0,0;1.5708rad)
  Rows = 1
  Support = -> [Fusion025]
FEATURE [Part::FeaturePython] Slice004  # WARN: FeaturePython — macro-defined, semantics opaque (R4)
  Base = -> Fusion025
  Mode = 1
  Tolerance = 0
  Tools = -> [Rectangle101]
FEATURE [Part::FeaturePython] Slice004_child0  label="Slice004.0"  # WARN: FeaturePython — macro-defined, semantics opaque (R4)
  Base = -> Slice004
  FilterType = 1
  Invert = false
  OverrideMaxVal = 0
  WindowFrom = 80
  WindowTo = 100
  items = 0
FEATURE [Part::Part2DObjectPython] Circle024  # Draft 2D object (typed FeaturePython)
  FirstAngle = 0
  LastAngle = 0
  MakeFace = true
  Placement = pos=(50.2687,87.7307,-2.1345) rot=(0,0,1;1.5708rad)
  Radius = 1.3
FEATURE [Part::Part2DObjectPython] Circle025  # Draft 2D object (typed FeaturePython)
  FirstAngle = 0
  LastAngle = 0
  MakeFace = true
  Placement = pos=(39.4687,87.7307,-2.1345) rot=(0,0,1;1.5708rad)
  Radius = 1.3
FEATURE [Part::Extrusion] Extrude130
  Base = -> Circle024
  Dir = (0,6e-15,1)
  DirMode = 2
  FaceMakerClass = Part::FaceMakerBullseye
  LengthFwd = 4.5
  LengthRev = 0
  Placement = pos=(0,0,-0.5) rot=(0,0,1;0rad)
  Solid = false
  Symmetric = false
FEATURE [Part::Extrusion] Extrude131
  Base = -> Circle025
  Dir = (0,6e-15,1)
  DirMode = 2
  FaceMakerClass = Part::FaceMakerBullseye
  LengthFwd = 4.5
  LengthRev = 0
  Placement = pos=(0,0,-0.5) rot=(0,0,1;0rad)
  Solid = false
  Symmetric = false
FEATURE [Part::MultiFuse] Fusion026
  Shapes = -> [Extrude131,Extrude130]
FEATURE [Part::Part2DObjectPython] Rectangle103  # Draft 2D object (typed FeaturePython)
  ChamferSize = 0
  Columns = 1
  FilletRadius = 0
  Height = 18
  Length = 5.8893
  MakeFace = true
  Placement = pos=(53.8687,84.786,1.8655) rot=(0,0,1;1.5708rad)
  Rows = 1
FEATURE [Part::Extrusion] Extrude132
  Base = -> Rectangle103
  Dir = (0,6e-15,1)
  DirMode = 2
  FaceMakerClass = Part::FaceMakerBullseye
  LengthFwd = -4
  LengthRev = 0
  Solid = false
  Symmetric = false
FEATURE [Part::Feature] Face037
  shape: bbox 26 x 6.04e-07 x 8.8 mm, 1 faces, 0 solids (baked)
FEATURE [Part::Extrusion] Extrusion036
  Base = -> Face037
  Dir = (0,90,-5.4e-13)
  DirMode = 0
  FaceMakerClass = Part::FaceMakerBullseye
  LengthFwd = 0
  LengthRev = 0
  Solid = true
  Symmetric = false
FEATURE [Part::Cut] Cut032018
  Base = -> Extrude132
  Tool = -> Fusion026
FEATURE [Part::Part2DObjectPython] Circle026  # Draft 2D object (typed FeaturePython)
  FirstAngle = 0
  LastAngle = 0
  MakeFace = true
  Placement = pos=(35.8687,-21.0369,9.86605) rot=(0.57735,0.57735,0.57735;2.0944rad)
  Radius = 12
FEATURE [Part::Part2DObjectPython] Rectangle105  # Draft 2D object (typed FeaturePython)
  ChamferSize = 0
  Columns = 1
  FilletRadius = 0
  Height = 12.0005
  Length = 12
  MakeFace = true
  Placement = pos=(35.8687,-33.0369,-2.1345) rot=(0.57735,0.57735,0.57735;2.0944rad)
  Rows = 1
FEATURE [Part::Extrusion] Extrusion037
  Base = -> Rectangle105
  Dir = (18,0,0)
  DirMode = 0
  FaceMakerClass = Part::FaceMakerBullseye
  LengthFwd = 0
  LengthRev = 0
  Solid = true
  Symmetric = false
FEATURE [Part::Extrusion] Extrusion038
  Base = -> Circle026
  Dir = (18,0,0)
  DirMode = 0
  FaceMakerClass = Part::FaceMakerBullseye
  LengthFwd = 0
  LengthRev = 0
  Solid = true
  Symmetric = false
FEATURE [Part::Cut] Cut032019
  Base = -> Extrusion037
  Tool = -> Extrusion038
FEATURE [Part::MultiFuse] Fusion027
  Shapes = -> [Slice004_child0,Cut032019]
FEATURE [Part::MultiFuse] Fusion028
  Shapes = -> [Cut032018,Extrusion036]
FEATURE [Part::MultiFuse] Fusion029
  Shapes = -> [Cut047_solid001,Fusion027,Fusion028]
FEATURE [Part::Feature] Fusion029001  label="Fusion030"
  Placement = pos=(-46.3247,0,-1.07e-14) rot=(0,0,1;0rad)
  shape: bbox 29 x 145.8 x 43 mm, 121 faces (baked)
